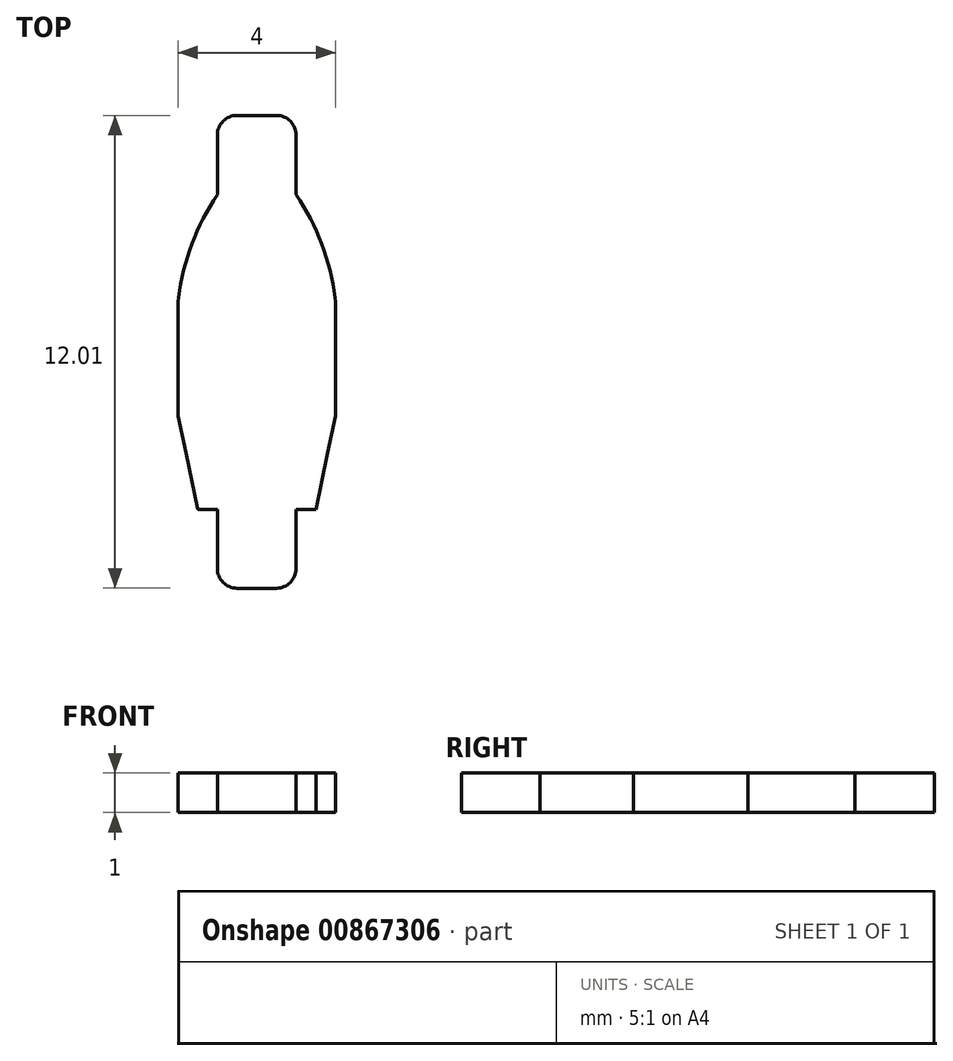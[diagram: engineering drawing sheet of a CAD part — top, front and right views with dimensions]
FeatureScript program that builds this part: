
annotation { "Feature Type Name" : "Feature", "Feature Type Description" : "" }
export const myFeature = defineFeature(function(context is Context, id is Id, definition is map)
    precondition{}
    {
        {
            var Q0;
            Q0=qCreatedBy(makeId("Top.planeOp"),FACE);
            var sketch = newSketch(context, id + "F0", { "sketchPlane" : qUnion([Q0])});
            skLineSegment(sketch, "E0", {"start": v(0, 0) * mm, "end": v(2, 0) * mm});
            skLineSegment(sketch, "E1", {"start": v(2, 0) * mm, "end": v(2, -0.01) * mm});
            skLineSegment(sketch, "E2", {"start": v(2, -0.01) * mm, "end": v(3, -0.01) * mm});
            skLineSegment(sketch, "E3", {"start": v(3, -0.01) * mm, "end": v(3, -8.01) * mm});
            skLineSegment(sketch, "E4", {"start": v(3, -8.01) * mm, "end": v(2, -8.01) * mm});
            skLineSegment(sketch, "E5", {"start": v(2, -8.01) * mm, "end": v(2, -10.01) * mm});
            skLineSegment(sketch, "E6", {"start": v(2, -10.01) * mm, "end": v(0, -10.01) * mm});
            skLineSegment(sketch, "E7", {"start": v(0, -10.01) * mm, "end": v(0, -8.01) * mm});
            skLineSegment(sketch, "E8", {"start": v(0, -8.01) * mm, "end": v(-1, -8.01) * mm});
            skLineSegment(sketch, "E9", {"start": v(-1, -8.01) * mm, "end": v(-1, -0.01) * mm});
            skLineSegment(sketch, "E10", {"start": v(-1, -0.01) * mm, "end": v(0, -0.01) * mm});
            skLineSegment(sketch, "E11", {"start": v(0, -0.01) * mm, "end": v(0, 0) * mm});
            skLineSegment(sketch, "E12", {"start": v(0, 0) * mm, "end": v(0, 2) * mm});
            skLineSegment(sketch, "E13", {"start": v(0, 2) * mm, "end": v(2, 2) * mm});
            skLineSegment(sketch, "E14", {"start": v(2, 2) * mm, "end": v(2, 0) * mm});
            skSolve(sketch);
        }
        {
            var Q0;
            Q0=makeQuery(id+"F0.imprint","IMPRINT",FACE,{"disambiguationData":[TD([[makeQuery(id+"F0.imprint","IMPRINT",EDGE,{"derivedFrom":sQuery(id+"F0.wireOp",EDGE,"E0")}),-1.0]])]});
            var Q1;
            Q1=makeQuery(id+"F0.imprint","IMPRINT",FACE,{"disambiguationData":[TD([[makeQuery(id+"F0.imprint","IMPRINT",EDGE,{"derivedFrom":sQuery(id+"F0.wireOp",EDGE,"E0")}),1.0]])]});
            extrude(context, id + "F1", {"entities" : qUnion([Q0, Q1]), "depth" : 1 * mm, "offsetDistance" : 25 * mm});
        }
        {
            var Q0;
            Q0=makeQuery(id+"F1.opExtrude","SWEPT_EDGE",EDGE,{"disambiguationData":[OSD([sQuery(id+"F0.wireOp",EDGE,"E3"),sQuery(id+"F0.wireOp",EDGE,"E4")])]});
            var Q1;
            Q1=makeQuery(id+"F1.opExtrude","SWEPT_EDGE",EDGE,{"disambiguationData":[OSD([sQuery(id+"F0.wireOp",EDGE,"E2"),sQuery(id+"F0.wireOp",EDGE,"E3")])]});
            var Q2;
            Q2=makeQuery(id+"F1.opExtrude","SWEPT_EDGE",EDGE,{"disambiguationData":[OSD([sQuery(id+"F0.wireOp",EDGE,"E9"),sQuery(id+"F0.wireOp",EDGE,"E10")])]});
            var Q3;
            Q3=makeQuery(id+"F1.opExtrude","SWEPT_EDGE",EDGE,{"disambiguationData":[OSD([sQuery(id+"F0.wireOp",EDGE,"E8"),sQuery(id+"F0.wireOp",EDGE,"E9")])]});
            var Q4;
            Q4=makeQuery(id+"F1.opExtrude","SWEPT_EDGE",EDGE,{"disambiguationData":[OSD([sQuery(id+"F0.wireOp",EDGE,"E13"),sQuery(id+"F0.wireOp",EDGE,"E14")])]});
            var Q5;
            Q5=makeQuery(id+"F1.opExtrude","SWEPT_EDGE",EDGE,{"disambiguationData":[OSD([sQuery(id+"F0.wireOp",EDGE,"E12"),sQuery(id+"F0.wireOp",EDGE,"E13")])]});
            var Q6;
            Q6=makeQuery(id+"F1.opExtrude","SWEPT_EDGE",EDGE,{"disambiguationData":[OSD([sQuery(id+"F0.wireOp",EDGE,"E5"),sQuery(id+"F0.wireOp",EDGE,"E6")])]});
            var Q7;
            Q7=makeQuery(id+"F1.opExtrude","SWEPT_EDGE",EDGE,{"disambiguationData":[OSD([sQuery(id+"F0.wireOp",EDGE,"E6"),sQuery(id+"F0.wireOp",EDGE,"E7")])]});
            fillet(context, id + "F2", {"entities" : qUnion([Q0, Q1, Q2, Q3, Q4, Q5, Q6, Q7]), "radius" : .5 * mm, "tangentPropagation" : true, "allowEdgeOverflow" : false});
        }
        {
            var Q0;
            Q0=makeQuery(id+"F1.opExtrude","CAP_FACE",FACE,{"disambiguationData":[OSD([sQuery(id+"F0.wireOp",EDGE,"E1"),sQuery(id+"F0.wireOp",EDGE,"E2"),sQuery(id+"F0.wireOp",EDGE,"E3"),sQuery(id+"F0.wireOp",EDGE,"E4"),sQuery(id+"F0.wireOp",EDGE,"E5"),sQuery(id+"F0.wireOp",EDGE,"E6"),sQuery(id+"F0.wireOp",EDGE,"E7"),sQuery(id+"F0.wireOp",EDGE,"E8"),sQuery(id+"F0.wireOp",EDGE,"E9"),sQuery(id+"F0.wireOp",EDGE,"E10"),sQuery(id+"F0.wireOp",EDGE,"E11"),sQuery(id+"F0.wireOp",EDGE,"E12"),sQuery(id+"F0.wireOp",EDGE,"E13"),sQuery(id+"F0.wireOp",EDGE,"E14")])],"isStart":false});
            var sketch = newSketch(context, id + "F3", { "sketchPlane" : qUnion([Q0])});
            skLineSegment(sketch, "E15", {"start": v(-0.5, -0.01) * mm, "end": v(-0.85, -1.57) * mm});
            skPoint(sketch, "E15.endSnap0", {"position": v(-0.85, -0.16) * mm});
            skLineSegment(sketch, "E16", {"start": v(-0.85, -1.57) * mm, "end": v(-1, -2.72) * mm});
            skLineSegment(sketch, "E17", {"start": v(1, 2) * mm, "end": v(1, -10.01) * mm, "construction": true});
            skLineSegment(sketch, "E18.MirrorCS", {"start": v(2.5, -0.01) * mm, "end": v(2.85, -1.57) * mm});
            skLineSegment(sketch, "E19.MirrorCS", {"start": v(2.85, -1.57) * mm, "end": v(3, -2.72) * mm});
            skSolve(sketch);
        }
        {
            var Q0;
            Q0 = qSketchRegion(id + "F3", true);
            var Q1;
            Q1=makeQuery(id+"F3.imprint","IMPRINT",FACE,{"disambiguationData":[TD([[makeQuery(id+"F3.imprint","IMPRINT",EDGE,{"derivedFrom":sQuery(id+"F3.wireOp",EDGE,"E15")}),-1.0]])]});
            var Q2;
            Q2=makeQuery(id+"F3.imprint","IMPRINT",FACE,{"disambiguationData":[TD([[makeQuery(id+"F3.imprint","IMPRINT",EDGE,{"derivedFrom":sQuery(id+"F3.wireOp",EDGE,"E18.MirrorCS")}),1.0]])]});
            extrude(context, id + "F4", {"entities" : qUnion([Q0, Q1, Q2]), "operationType" : NewBodyOperationType.REMOVE, "oppositeDirection" : true, "depth" : 25 * mm, "offsetDistance" : 25 * mm});
        }
        {
            var Q0;
            {var subQ0=sQuery(id+"F0.wireOp",EDGE,"E10");var subQ1=sQuery(id+"F0.wireOp",EDGE,"E9");Q0=makeQuery(id+"F4.boolean.opBoolean","MERGE",EDGE,{"derivedFrom":[makeQuery(id+"F2.opFillet","BLEND_EDGE",EDGE,{"blendedFrom":[makeQuery(id+"F1.opExtrude","SWEPT_EDGE",EDGE,{"disambiguationData":[OSD([subQ1,subQ0])]}),makeQuery(id+"F1.opExtrude","SWEPT_FACE",FACE,{"disambiguationData":[OSD([subQ0])]})],"blendedInto":[makeQuery(id+"F1.opExtrude","SWEPT_FACE",FACE,{"disambiguationData":[OSD([subQ0])]})]})],"fromTools":[makeQuery(id+"F4.opExtrude","SWEPT_EDGE",EDGE,{"disambiguationData":[OSD([sQuery(id+"F0.wireOp",EDGE,"E1"),sQuery(id+"F0.wireOp",EDGE,"E2"),sQuery(id+"F0.wireOp",EDGE,"E3"),sQuery(id+"F0.wireOp",EDGE,"E4"),sQuery(id+"F0.wireOp",EDGE,"E5"),sQuery(id+"F0.wireOp",EDGE,"E6"),sQuery(id+"F0.wireOp",EDGE,"E7"),sQuery(id+"F0.wireOp",EDGE,"E8"),subQ1,subQ0,sQuery(id+"F0.wireOp",EDGE,"E11"),sQuery(id+"F0.wireOp",EDGE,"E12"),sQuery(id+"F0.wireOp",EDGE,"E13"),sQuery(id+"F0.wireOp",EDGE,"E14"),sQuery(id+"F3.wireOp",EDGE,"E15")])]})]});}
            var Q1;
            Q1=makeQuery(id+"F4.boolean.opBoolean","COPY",EDGE,{"derivedFrom":makeQuery(id+"F4.opExtrude","SWEPT_EDGE",EDGE,{"disambiguationData":[OSD([sQuery(id+"F0.wireOp",EDGE,"E9"),sQuery(id+"F3.wireOp",EDGE,"E16")])]})});
            var Q2;
            {var subQ0=sQuery(id+"F0.wireOp",EDGE,"E3");var subQ1=sQuery(id+"F0.wireOp",EDGE,"E2");Q2=makeQuery(id+"F4.boolean.opBoolean","MERGE",EDGE,{"derivedFrom":[makeQuery(id+"F2.opFillet","BLEND_EDGE",EDGE,{"blendedFrom":[makeQuery(id+"F1.opExtrude","SWEPT_EDGE",EDGE,{"disambiguationData":[OSD([subQ1,subQ0])]}),makeQuery(id+"F1.opExtrude","SWEPT_FACE",FACE,{"disambiguationData":[OSD([subQ1])]})],"blendedInto":[makeQuery(id+"F1.opExtrude","SWEPT_FACE",FACE,{"disambiguationData":[OSD([subQ1])]})]})],"fromTools":[makeQuery(id+"F4.opExtrude","SWEPT_EDGE",EDGE,{"disambiguationData":[OSD([sQuery(id+"F0.wireOp",EDGE,"E1"),subQ1,subQ0,sQuery(id+"F0.wireOp",EDGE,"E4"),sQuery(id+"F0.wireOp",EDGE,"E5"),sQuery(id+"F0.wireOp",EDGE,"E6"),sQuery(id+"F0.wireOp",EDGE,"E7"),sQuery(id+"F0.wireOp",EDGE,"E8"),sQuery(id+"F0.wireOp",EDGE,"E9"),sQuery(id+"F0.wireOp",EDGE,"E10"),sQuery(id+"F0.wireOp",EDGE,"E11"),sQuery(id+"F0.wireOp",EDGE,"E12"),sQuery(id+"F0.wireOp",EDGE,"E13"),sQuery(id+"F0.wireOp",EDGE,"E14"),sQuery(id+"F3.wireOp",EDGE,"E18.MirrorCS")])]})]});}
            var Q3;
            Q3=makeQuery(id+"F4.boolean.opBoolean","COPY",EDGE,{"derivedFrom":makeQuery(id+"F4.opExtrude","SWEPT_EDGE",EDGE,{"disambiguationData":[OSD([sQuery(id+"F0.wireOp",EDGE,"E3"),sQuery(id+"F3.wireOp",EDGE,"E19.MirrorCS")])]})});
            fillet(context, id + "F5", {"entities" : qUnion([Q0, Q1, Q2, Q3]), "radius" : 6 * mm, "tangentPropagation" : true, "allowEdgeOverflow" : false});
        }
        {
            var Q0;
            Q0=makeQuery(id+"F1.opExtrude","CAP_FACE",FACE,{"disambiguationData":[OSD([sQuery(id+"F0.wireOp",EDGE,"E1"),sQuery(id+"F0.wireOp",EDGE,"E2"),sQuery(id+"F0.wireOp",EDGE,"E3"),sQuery(id+"F0.wireOp",EDGE,"E4"),sQuery(id+"F0.wireOp",EDGE,"E5"),sQuery(id+"F0.wireOp",EDGE,"E6"),sQuery(id+"F0.wireOp",EDGE,"E7"),sQuery(id+"F0.wireOp",EDGE,"E8"),sQuery(id+"F0.wireOp",EDGE,"E9"),sQuery(id+"F0.wireOp",EDGE,"E10"),sQuery(id+"F0.wireOp",EDGE,"E11"),sQuery(id+"F0.wireOp",EDGE,"E12"),sQuery(id+"F0.wireOp",EDGE,"E13"),sQuery(id+"F0.wireOp",EDGE,"E14")])],"isStart":false});
            var sketch = newSketch(context, id + "F6", { "sketchPlane" : qUnion([Q0])});
            skLineSegment(sketch, "E20", {"start": v(-0.5, -8.01) * mm, "end": v(-0.8, -6.58) * mm});
            skLineSegment(sketch, "E21", {"start": v(-0.8, -6.58) * mm, "end": v(-1, -5.64) * mm});
            skLineSegment(sketch, "E22", {"start": v(1, 2) * mm, "end": v(1, -10.01) * mm, "construction": true});
            skLineSegment(sketch, "E23.MirrorCS", {"start": v(2.5, -8.01) * mm, "end": v(2.8, -6.58) * mm});
            skLineSegment(sketch, "E24.MirrorCS", {"start": v(2.8, -6.58) * mm, "end": v(3, -5.64) * mm});
            skSolve(sketch);
        }
        {
            var Q0;
            Q0 = qSketchRegion(id + "F6", true);
            var Q1;
            Q1=makeQuery(id+"F6.imprint","IMPRINT",FACE,{"disambiguationData":[TD([[makeQuery(id+"F6.imprint","IMPRINT",EDGE,{"derivedFrom":sQuery(id+"F6.wireOp",EDGE,"E20")}),1.0]])]});
            var Q2;
            Q2=makeQuery(id+"F6.imprint","IMPRINT",FACE,{"disambiguationData":[TD([[makeQuery(id+"F6.imprint","IMPRINT",EDGE,{"derivedFrom":sQuery(id+"F6.wireOp",EDGE,"E23.MirrorCS")}),-1.0]])]});
            extrude(context, id + "F7", {"entities" : qUnion([Q0, Q1, Q2]), "operationType" : NewBodyOperationType.REMOVE, "oppositeDirection" : true, "depth" : 25 * mm, "offsetDistance" : 25 * mm});
        }
        {
            var Q0;
            Q0=makeQuery(id+"F7.boolean.opBoolean","COPY",EDGE,{"derivedFrom":makeQuery(id+"F7.opExtrude","SWEPT_EDGE",EDGE,{"disambiguationData":[OSD([sQuery(id+"F0.wireOp",EDGE,"E3"),sQuery(id+"F6.wireOp",EDGE,"E24.MirrorCS")])]})});
            var Q1;
            Q1=makeQuery(id+"F7.boolean.opBoolean","COPY",EDGE,{"derivedFrom":makeQuery(id+"F7.opExtrude","SWEPT_EDGE",EDGE,{"disambiguationData":[OSD([sQuery(id+"F0.wireOp",EDGE,"E9"),sQuery(id+"F6.wireOp",EDGE,"E21")])]})});
            var Q2;
            {var subQ0=sQuery(id+"F0.wireOp",EDGE,"E9");var subQ1=sQuery(id+"F0.wireOp",EDGE,"E8");Q2=makeQuery(id+"F7.boolean.opBoolean","MERGE",EDGE,{"derivedFrom":[makeQuery(id+"F2.opFillet","BLEND_EDGE",EDGE,{"blendedFrom":[makeQuery(id+"F1.opExtrude","SWEPT_EDGE",EDGE,{"disambiguationData":[OSD([subQ1,subQ0])]}),makeQuery(id+"F1.opExtrude","SWEPT_FACE",FACE,{"disambiguationData":[OSD([subQ1])]})],"blendedInto":[makeQuery(id+"F1.opExtrude","SWEPT_FACE",FACE,{"disambiguationData":[OSD([subQ1])]})]})],"fromTools":[makeQuery(id+"F7.opExtrude","SWEPT_EDGE",EDGE,{"disambiguationData":[OSD([sQuery(id+"F0.wireOp",EDGE,"E1"),sQuery(id+"F0.wireOp",EDGE,"E2"),sQuery(id+"F0.wireOp",EDGE,"E3"),sQuery(id+"F0.wireOp",EDGE,"E4"),sQuery(id+"F0.wireOp",EDGE,"E5"),sQuery(id+"F0.wireOp",EDGE,"E6"),sQuery(id+"F0.wireOp",EDGE,"E7"),subQ1,subQ0,sQuery(id+"F0.wireOp",EDGE,"E10"),sQuery(id+"F0.wireOp",EDGE,"E11"),sQuery(id+"F0.wireOp",EDGE,"E12"),sQuery(id+"F0.wireOp",EDGE,"E13"),sQuery(id+"F0.wireOp",EDGE,"E14"),sQuery(id+"F6.wireOp",EDGE,"E20")])]})]});}
            fillet(context, id + "F8", {"entities" : qUnion([Q0, Q1, Q2]), "radius" : 0.03 * mm, "tangentPropagation" : true, "allowEdgeOverflow" : false});
        }
    });
